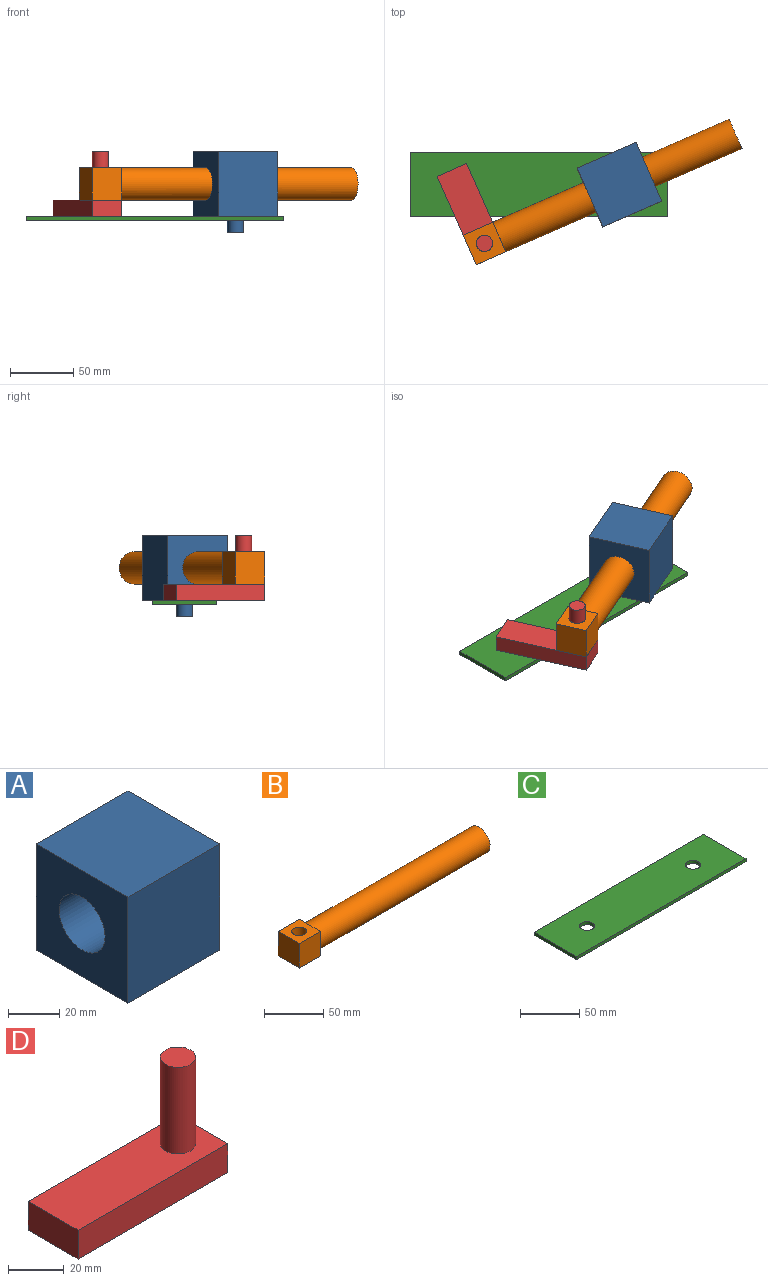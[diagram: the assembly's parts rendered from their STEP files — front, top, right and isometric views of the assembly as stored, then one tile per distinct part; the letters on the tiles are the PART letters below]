
ASSEMBLY  parts=4 mates=7
PART A: 9 faces, bbox 50.8x50.8x63.5 mm
  f0: plane 50.8x50.8mm, normal (0,0,1), area 2580.6mm2, adj f1,f4,f5,f6
  f1: plane 50.8x50.8mm, normal (0,-1,0), area 2580.6mm2, adj f0,f2,f5,f6
  f2: plane 50.8x50.8mm, normal (0,0,-1), area 2454mm2, adj f1,f4,f5,f6,f7
  f3: cylinder r=12.7mm len=50.8mm, axis (-1,0,0), area 4053.7mm2, adj f5,f6
  f4: plane 50.8x50.8mm, normal (0,1,0), area 2580.6mm2, adj f0,f2,f5,f6
  f5: plane 50.8x50.8mm, normal (1,0,0), area 2073.9mm2, adj f0,f1,f2,f3,f4
  f6: plane 50.8x50.8mm, normal (-1,0,0), area 2073.9mm2, adj f0,f1,f2,f3,f4
  f7: cylinder r=6.35mm len=12.7mm, axis (0,0,1), area 506.7mm2, adj f2,f8
  f8: plane 12.7x12.7mm, normal (0,0,-1), area 126.7mm2, adj f7
PART B: 12 faces, bbox 228.6x25.4x25.4 mm
  f0: plane 12.7x12.7mm, normal (1,0,0), area 34.6mm2, adj f3,f8,f10
  f1: plane 12.7x12.7mm, normal (1,0,0), area 34.6mm2, adj f5,f8,f10
  f2: plane 12.7x12.7mm, normal (1,0,0), area 34.6mm2, adj f5,f9,f10
  f3: plane 25.4x25.4mm, normal (0,1,0), area 645.2mm2, adj f0,f4,f7,f8,f9
  f4: plane 25.4x25.4mm, normal (-1,0,0), area 645.2mm2, adj f3,f5,f8,f9
  f5: plane 25.4x25.4mm, normal (0,-1,0), area 645.2mm2, adj f1,f2,f4,f8,f9
  f6: cylinder r=6.35mm len=25.4mm, axis (0,0,-1), area 1013.4mm2, adj f8,f9
  f7: plane 12.7x12.7mm, normal (1,0,0), area 34.6mm2, adj f3,f9,f10
  f8: plane 25.4x25.4mm, normal (0,0,1), area 518.5mm2, adj f0,f1,f3,f4,f5,f6
  f9: plane 25.4x25.4mm, normal (0,0,-1), area 518.5mm2, adj f2,f3,f4,f5,f6,f7
  f10: cylinder r=12.7mm len=203.2mm, axis (-1,0,0), area 16214.6mm2, adj f0,f1,f2,f7,f11
  f11: plane 25.4x25.4mm, normal (1,0,0), area 506.7mm2, adj f10
PART C: 8 faces, bbox 203.2x50.8x3.2 mm
  f0: plane 203.2x3.18mm, normal (0,-1,0), area 645.2mm2, adj f1,f5,f6,f7
  f1: plane 50.8x3.18mm, normal (1,0,0), area 161.3mm2, adj f0,f2,f6,f7
  f2: plane 203.2x3.18mm, normal (0,1,0), area 645.2mm2, adj f1,f5,f6,f7
  f3: cylinder r=6.35mm len=12.7mm, axis (0,0,-1), area 126.7mm2, adj f6,f7
  f4: cylinder r=6.35mm len=12.7mm, axis (0,0,-1), area 126.7mm2, adj f6,f7
  f5: plane 50.8x3.18mm, normal (-1,0,0), area 161.3mm2, adj f0,f2,f6,f7
  f6: plane 203.2x50.8mm, normal (0,0,1), area 10069.2mm2, adj f0,f1,f2,f3,f4,f5
  f7: plane 203.2x50.8mm, normal (0,0,-1), area 10069.2mm2, adj f0,f1,f2,f3,f4,f5
PART D: 10 faces, bbox 76.2x25.4x54 mm
  f0: plane 25.4x12.7mm, normal (1,0,0), area 322.6mm2, adj f1,f3,f4,f5
  f1: plane 76.2x12.7mm, normal (0,1,0), area 967.7mm2, adj f0,f2,f4,f5
  f2: plane 25.4x12.7mm, normal (-1,0,0), area 322.6mm2, adj f1,f3,f4,f5
  f3: plane 76.2x12.7mm, normal (0,-1,0), area 967.7mm2, adj f0,f2,f4,f5
  f4: plane 76.2x25.4mm, normal (0,0,1), area 1808.8mm2, adj f0,f1,f2,f3,f6
  f5: plane 76.2x25.4mm, normal (0,0,-1), area 1808.8mm2, adj f0,f1,f2,f3,f8
  f6: cylinder r=6.35mm len=38.1mm, axis (0,0,-1), area 1520.1mm2, adj f4,f7
  f7: plane 12.7x12.7mm, normal (0,0,1), area 126.7mm2, adj f6
  f8: cylinder r=6.35mm len=12.7mm, axis (0,0,1), area 126.7mm2, adj f5,f9
  f9: plane 12.7x12.7mm, normal (0,0,-1), area 126.7mm2, adj f8
PLACE A rot(axis=(0,0,1),23.6deg) t=(41.86,1.92,27.47)mm
PLACE B rot(axis=(0,0,1),23.6deg) t=(-41.25,-34.35,14.77)mm
PLACE C t=(1.64,12.08,-1.11)mm fixed
PLACE D rot(axis=(0,0,-1),66.1deg) t=(-51.56,-11.14,2.07)mm
MATE planar A.f7 <-> C.f6  axis (0,0,-1) through (65.14,12.08,2.07)mm
MATE cylindrical B.f6 <-> D.f6  axis (0,0,1) through (-41.25,-34.35,40.17)mm
MATE planar B.f6 <-> D.f4  axis (0,0,-1) through (-41.25,-34.35,14.77)mm
MATE cylindrical D.f8 <-> C.f3  axis (0,0,-1) through (-61.86,12.08,-1.11)mm
MATE planar D.f5 <-> C.f6  axis (0,0,-1) through (-50.84,-12.76,2.07)mm
MATE cylindrical A.f7 <-> C.f4  axis (0,0,1) through (65.14,12.08,-4.28)mm
MATE cylindrical A.f3 <-> B.f10  axis (-0.92,-0.4,0) through (88.42,22.24,27.47)mm
